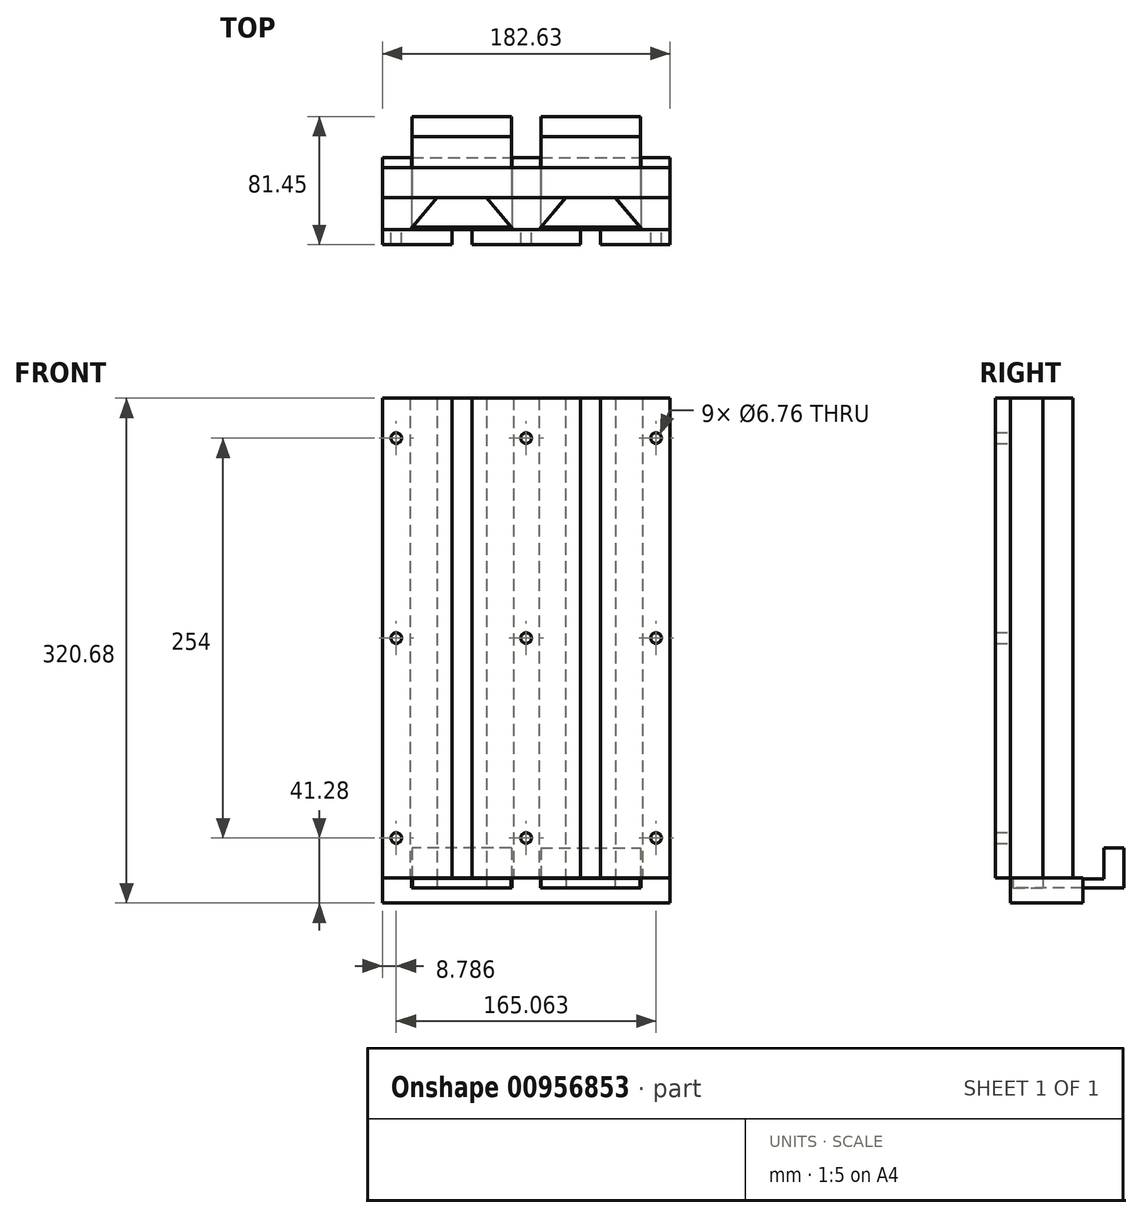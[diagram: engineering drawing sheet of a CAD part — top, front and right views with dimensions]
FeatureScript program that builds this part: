
annotation { "Feature Type Name" : "Feature", "Feature Type Description" : "" }
export const myFeature = defineFeature(function(context is Context, id is Id, definition is map)
    precondition{}
    {
        {
            var Q0;
            Q0=qCreatedBy(makeId("Top.planeOp"),FACE);
            var sketch = newSketch(context, id + "F0", { "sketchPlane" : qUnion([Q0])});
            skLineSegment(sketch, "E0", {"start": v(-15.74, -18.9) * mm, "end": v(0, 0) * mm});
            skLineSegment(sketch, "E1", {"start": v(0, 0) * mm, "end": v(31.27, 0) * mm});
            skLineSegment(sketch, "E2", {"start": v(31.27, 0) * mm, "end": v(47, -18.9) * mm});
            skLineSegment(sketch, "E3", {"start": v(47, -18.9) * mm, "end": v(-15.74, -18.9) * mm});
            skLineSegment(sketch, "E4", {"start": v(66.05, -18.9) * mm, "end": v(81.79, 0) * mm});
            skLineSegment(sketch, "E5", {"start": v(81.79, 0) * mm, "end": v(113.06, 0) * mm});
            skLineSegment(sketch, "E6", {"start": v(113.06, 0) * mm, "end": v(128.8, -18.9) * mm});
            skLineSegment(sketch, "E7", {"start": v(128.8, -18.9) * mm, "end": v(66.05, -18.9) * mm});
            skSolve(sketch);
        }
        {
            var Q0;
            Q0 = qSketchRegion(id + "F0", true);
            extrude(context, id + "F1", {"entities" : qUnion([Q0]), "depth" : 5.97 * mm, "offsetDistance" : 25.4 * mm});
        }
        {
            var Q0;
            Q0=makeQuery(id+"F1.opExtrude","CAP_FACE",FACE,{"disambiguationData":[OSD([sQuery(id+"F0.wireOp",EDGE,"E4"),sQuery(id+"F0.wireOp",EDGE,"E5"),sQuery(id+"F0.wireOp",EDGE,"E6"),sQuery(id+"F0.wireOp",EDGE,"E7")])],"isStart":true});
            var sketch = newSketch(context, id + "F2", { "sketchPlane" : qUnion([Q0])});
            skLineSegment(sketch, "E8.bottom", {"start": v(-34.79, 20.49) * mm, "end": v(147.84, 20.49) * mm});
            skLineSegment(sketch, "E8.top", {"start": v(-34.79, -25.4) * mm, "end": v(147.84, -25.4) * mm});
            skLineSegment(sketch, "E8.left", {"start": v(-34.79, 20.49) * mm, "end": v(-34.79, -25.4) * mm});
            skLineSegment(sketch, "E8.right", {"start": v(147.84, 20.49) * mm, "end": v(147.84, -25.4) * mm});
            skSolve(sketch);
        }
        {
            var Q0;
            Q0 = qSketchRegion(id + "F2", true);
            extrude(context, id + "F3", {"entities" : qUnion([Q0]), "depth" : 9.52 * mm, "offsetDistance" : 25.4 * mm});
        }
        {
            var Q0;
            Q0=makeQuery(id+"F1.opExtrude","SWEPT_FACE",FACE,{"disambiguationData":[OSD([sQuery(id+"F0.wireOp",EDGE,"E5")])]});
            var sketch = newSketch(context, id + "F4", { "sketchPlane" : qUnion([Q0])});
            skLineSegment(sketch, "E9.0", {"start": v(-128.8, 5.97) * mm, "end": v(-128.8, 0) * mm, "construction": true});
            skLineSegment(sketch, "E10.0", {"start": v(-113.06, 5.97) * mm, "end": v(-128.8, 5.97) * mm, "construction": true});
            skLineSegment(sketch, "E11.0", {"start": v(-81.79, 5.97) * mm, "end": v(-113.06, 5.97) * mm, "construction": true});
            skLineSegment(sketch, "E12.0", {"start": v(-66.05, 5.97) * mm, "end": v(-81.79, 5.97) * mm, "construction": true});
            skLineSegment(sketch, "E13.0", {"start": v(-66.05, 5.97) * mm, "end": v(-66.05, 0) * mm, "construction": true});
            skLineSegment(sketch, "E14.0", {"start": v(-47, 5.97) * mm, "end": v(-47, 0) * mm, "construction": true});
            skLineSegment(sketch, "E15.0", {"start": v(-31.27, 5.97) * mm, "end": v(-47, 5.97) * mm, "construction": true});
            skLineSegment(sketch, "E16.0", {"start": v(-31.27, 5.97) * mm, "end": v(-31.27, 0) * mm});
            skLineSegment(sketch, "E17.0", {"start": v(0, 5.97) * mm, "end": v(-31.27, 5.97) * mm, "construction": true});
            skLineSegment(sketch, "E18.0", {"start": v(15.74, 5.97) * mm, "end": v(0, 5.97) * mm, "construction": true});
            skLineSegment(sketch, "E19.0", {"start": v(15.74, 5.97) * mm, "end": v(15.74, 0) * mm, "construction": true});
            skLineSegment(sketch, "E20", {"start": v(-129.04, 0) * mm, "end": v(-129.04, 5.71) * mm});
            skLineSegment(sketch, "E21", {"start": v(-129.04, 5.71) * mm, "end": v(-65.8, 5.72) * mm});
            skLineSegment(sketch, "E22", {"start": v(-65.8, 5.72) * mm, "end": v(-65.8, 0) * mm});
            skLineSegment(sketch, "E23", {"start": v(-65.8, 0) * mm, "end": v(-129.04, 0) * mm});
            skLineSegment(sketch, "E24", {"start": v(-47.26, 0) * mm, "end": v(-47.26, 5.72) * mm});
            skLineSegment(sketch, "E25", {"start": v(-47.26, 5.72) * mm, "end": v(15.99, 5.72) * mm});
            skLineSegment(sketch, "E26", {"start": v(15.99, 5.72) * mm, "end": v(15.99, 0) * mm});
            skLineSegment(sketch, "E27", {"start": v(15.99, 0) * mm, "end": v(-47.26, 0) * mm});
            skSolve(sketch);
        }
        {
            var Q0;
            Q0 = qSketchRegion(id + "F4", true);
            extrude(context, id + "F5", {"entities" : qUnion([Q0]), "depth" : 25.4 * mm, "offsetDistance" : 25.4 * mm});
        }
        {
            var Q0;
            Q0=makeQuery(id+"F3.opExtrude","CAP_FACE",FACE,{"disambiguationData":[OSD([sQuery(id+"F2.wireOp",EDGE,"E8.bottom"),sQuery(id+"F2.wireOp",EDGE,"E8.top"),sQuery(id+"F2.wireOp",EDGE,"E8.left"),sQuery(id+"F2.wireOp",EDGE,"E8.right")])],"isStart":true});
            var sketch = newSketch(context, id + "F6", { "sketchPlane" : qUnion([Q0])});
            skLineSegment(sketch, "E28.bottom", {"start": v(-34.79, 25.4) * mm, "end": v(-16.24, 25.4) * mm});
            skLineSegment(sketch, "E28.top", {"start": v(-34.79, -20.49) * mm, "end": v(-16.24, -20.49) * mm});
            skLineSegment(sketch, "E28.left", {"start": v(-34.79, 25.4) * mm, "end": v(-34.79, -20.49) * mm});
            skLineSegment(sketch, "E28.right", {"start": v(-16.24, 25.4) * mm, "end": v(-16.24, -20.49) * mm});
            skLineSegment(sketch, "E29.bottom", {"start": v(147.84, 25.4) * mm, "end": v(129.3, 25.4) * mm});
            skLineSegment(sketch, "E29.top", {"start": v(147.84, -20.49) * mm, "end": v(129.3, -20.49) * mm});
            skLineSegment(sketch, "E29.left", {"start": v(147.84, 25.4) * mm, "end": v(147.84, -20.49) * mm});
            skLineSegment(sketch, "E29.right", {"start": v(129.3, 25.4) * mm, "end": v(129.3, -20.49) * mm});
            skLineSegment(sketch, "E30.bottom", {"start": v(47.51, 25.4) * mm, "end": v(65.54, 25.4) * mm});
            skLineSegment(sketch, "E30.top", {"start": v(47.51, -20.49) * mm, "end": v(65.54, -20.49) * mm});
            skLineSegment(sketch, "E30.left", {"start": v(47.51, 25.4) * mm, "end": v(47.51, -20.49) * mm});
            skLineSegment(sketch, "E30.right", {"start": v(65.54, 25.4) * mm, "end": v(65.54, -20.49) * mm});
            skSolve(sketch);
        }
        {
            var Q0;
            Q0 = qSketchRegion(id + "F6", true);
            extrude(context, id + "F7", {"entities" : qUnion([Q0]), "operationType" : NewBodyOperationType.ADD, "depth" : 6.35 * mm, "offsetDistance" : 25.4 * mm});
        }
        {
            var Q0;
            Q0=makeQuery(id+"F7.opExtrude","CAP_FACE",FACE,{"disambiguationData":[OSD([sQuery(id+"F6.wireOp",EDGE,"E30.bottom"),sQuery(id+"F6.wireOp",EDGE,"E30.top"),sQuery(id+"F6.wireOp",EDGE,"E30.left"),sQuery(id+"F6.wireOp",EDGE,"E30.right")])],"isStart":false});
            var sketch = newSketch(context, id + "F8", { "sketchPlane" : qUnion([Q0])});
            skLineSegment(sketch, "E31.0", {"start": v(-34.79, -20.49) * mm, "end": v(-34.79, 25.4) * mm, "construction": true});
            skLineSegment(sketch, "E32.0", {"start": v(147.84, -20.49) * mm, "end": v(147.84, 25.4) * mm, "construction": true});
            skLineSegment(sketch, "E33.0", {"start": v(-34.79, 25.4) * mm, "end": v(-16.24, 25.4) * mm, "construction": true});
            skLineSegment(sketch, "E34.0", {"start": v(129.3, 25.4) * mm, "end": v(147.84, 25.4) * mm, "construction": true});
            skPoint(sketch, "E35.0", {"position": v(56.53, 25.4) * mm});
            skLineSegment(sketch, "E36.bottom", {"start": v(-34.79, 19.05) * mm, "end": v(147.84, 19.05) * mm});
            skLineSegment(sketch, "E36.top", {"start": v(-34.79, 0) * mm, "end": v(147.84, 0) * mm});
            skLineSegment(sketch, "E36.left", {"start": v(-34.79, 19.05) * mm, "end": v(-34.79, 0) * mm});
            skLineSegment(sketch, "E36.right", {"start": v(147.84, 19.05) * mm, "end": v(147.84, 0) * mm});
            skSolve(sketch);
        }
        {
            var Q0;
            Q0 = qSketchRegion(id + "F8", true);
            extrude(context, id + "F9", {"entities" : qUnion([Q0]), "depth" : 304.8 * mm, "offsetDistance" : 25.4 * mm});
        }
        {
            var Q0;
            Q0=makeQuery(id+"F5.opExtrude","SWEPT_FACE",FACE,{"disambiguationData":[OSD([sQuery(id+"F4.wireOp",EDGE,"E26")])]});
            var sketch = newSketch(context, id + "F10", { "sketchPlane" : qUnion([Q0])});
            skLineSegment(sketch, "E37.bottom", {"start": v(-51.44, 25.4) * mm, "end": v(-38.74, 25.4) * mm});
            skLineSegment(sketch, "E37.top", {"start": v(-51.44, 0) * mm, "end": v(-38.74, 0) * mm});
            skLineSegment(sketch, "E37.left", {"start": v(-51.44, 25.4) * mm, "end": v(-51.44, 0) * mm});
            skLineSegment(sketch, "E37.right", {"start": v(-38.74, 25.4) * mm, "end": v(-38.74, 5.72) * mm});
            skLineSegment(sketch, "E38.bottom", {"start": v(-38.74, 0) * mm, "end": v(-25.4, 0) * mm});
            skLineSegment(sketch, "E38.top", {"start": v(-38.74, 5.72) * mm, "end": v(-25.4, 5.72) * mm});
            skLineSegment(sketch, "E38.right", {"start": v(-25.4, 0) * mm, "end": v(-25.4, 5.72) * mm});
            skSolve(sketch);
        }
        {
            var Q0;
            Q0 = qSketchRegion(id + "F10", true);
            var Q1;
            Q1=makeQuery(id+"F5.opExtrude","SWEPT_FACE",FACE,{"disambiguationData":[OSD([sQuery(id+"F4.wireOp",EDGE,"E24")])]});
            extrude(context, id + "F11", {"entities" : qUnion([Q0]), "operationType" : NewBodyOperationType.ADD, "endBound" : BoundingType.UP_TO_SURFACE, "oppositeDirection" : true, "depth" : 25.4 * mm, "endBoundEntityFace" : qUnion([Q1]), "offsetDistance" : 25.4 * mm});
        }
        {
            var Q0;
            Q0=makeQuery(id+"F5.opExtrude","SWEPT_FACE",FACE,{"disambiguationData":[OSD([sQuery(id+"F4.wireOp",EDGE,"E20")])]});
            var sketch = newSketch(context, id + "F12", { "sketchPlane" : qUnion([Q0])});
            skLineSegment(sketch, "E39.0", {"start": v(38.74, 5.72) * mm, "end": v(25.4, 5.72) * mm});
            skLineSegment(sketch, "E39.1", {"start": v(38.74, 0) * mm, "end": v(25.4, 0) * mm});
            skLineSegment(sketch, "E39.2", {"start": v(51.44, 0) * mm, "end": v(38.74, 0) * mm});
            skLineSegment(sketch, "E39.3", {"start": v(25.4, 0) * mm, "end": v(25.4, 5.72) * mm});
            skLineSegment(sketch, "E39.4", {"start": v(51.44, 25.4) * mm, "end": v(51.44, 0) * mm});
            skLineSegment(sketch, "E39.5", {"start": v(38.74, 25.4) * mm, "end": v(38.74, 5.72) * mm});
            skLineSegment(sketch, "E39.6", {"start": v(51.44, 25.4) * mm, "end": v(38.74, 25.4) * mm});
            skSolve(sketch);
        }
        {
            var Q0;
            Q0 = qSketchRegion(id + "F12", true);
            var Q1;
            Q1=makeQuery(id+"F5.opExtrude","SWEPT_FACE",FACE,{"disambiguationData":[OSD([sQuery(id+"F4.wireOp",EDGE,"E22")])]});
            extrude(context, id + "F13", {"entities" : qUnion([Q0]), "operationType" : NewBodyOperationType.ADD, "endBound" : BoundingType.UP_TO_SURFACE, "oppositeDirection" : true, "depth" : 25.4 * mm, "endBoundEntityFace" : qUnion([Q1]), "offsetDistance" : 25.4 * mm});
        }
        {
            var Q0;
            Q0=makeQuery(id+"F7.opExtrude","CAP_FACE",FACE,{"disambiguationData":[OSD([sQuery(id+"F6.wireOp",EDGE,"E30.bottom"),sQuery(id+"F6.wireOp",EDGE,"E30.top"),sQuery(id+"F6.wireOp",EDGE,"E30.left"),sQuery(id+"F6.wireOp",EDGE,"E30.right")])],"isStart":false});
            var sketch = newSketch(context, id + "F14", { "sketchPlane" : qUnion([Q0])});
            skLineSegment(sketch, "E40", {"start": v(-34.79, 0) * mm, "end": v(-34.79, -20.49) * mm});
            skLineSegment(sketch, "E41", {"start": v(-34.79, -20.49) * mm, "end": v(-17.22, -20.49) * mm});
            skLineSegment(sketch, "E42", {"start": v(-17.22, -20.49) * mm, "end": v(-0.17, 0) * mm});
            skLineSegment(sketch, "E43", {"start": v(-0.17, 0) * mm, "end": v(-34.79, 0) * mm});
            skLineSegment(sketch, "E44", {"start": v(56.53, 25.4) * mm, "end": v(56.53, -20.49) * mm, "construction": true});
            skLineSegment(sketch, "E45", {"start": v(31.43, 0) * mm, "end": v(48.49, -20.49) * mm});
            skLineSegment(sketch, "E46", {"start": v(48.49, -20.49) * mm, "end": v(56.53, -20.49) * mm});
            skLineSegment(sketch, "E47", {"start": v(56.53, 0) * mm, "end": v(31.43, 0) * mm});
            skLineSegment(sketch, "E48.MirrorCS", {"start": v(64.57, -20.49) * mm, "end": v(56.53, -20.49) * mm});
            skLineSegment(sketch, "E49.MirrorCS", {"start": v(56.53, 0) * mm, "end": v(81.62, 0) * mm});
            skLineSegment(sketch, "E50.MirrorCS", {"start": v(81.62, 0) * mm, "end": v(64.57, -20.49) * mm});
            skLineSegment(sketch, "E51.MirrorCS", {"start": v(130.28, -20.49) * mm, "end": v(113.22, 0) * mm});
            skLineSegment(sketch, "E52.MirrorCS", {"start": v(147.84, -20.49) * mm, "end": v(130.28, -20.49) * mm});
            skLineSegment(sketch, "E53.MirrorCS", {"start": v(113.22, 0) * mm, "end": v(147.84, 0) * mm});
            skLineSegment(sketch, "E54.MirrorCS", {"start": v(147.84, 0) * mm, "end": v(147.84, -20.49) * mm});
            skSolve(sketch);
        }
        {
            var Q0;
            Q0 = qSketchRegion(id + "F14", true);
            extrude(context, id + "F15", {"entities" : qUnion([Q0]), "depth" : 304.8 * mm, "offsetDistance" : 25.4 * mm});
        }
        {
            var Q0;
            Q0=makeQuery(id+"F15.opExtrude","SWEPT_FACE",FACE,{"disambiguationData":[OSD([sQuery(id+"F14.wireOp",EDGE,"E41")])]});
            var sketch = newSketch(context, id + "F16", { "sketchPlane" : qUnion([Q0])});
            skLineSegment(sketch, "E55.bottom", {"start": v(-34.79, 311.15) * mm, "end": v(9.28, 311.15) * mm});
            skLineSegment(sketch, "E55.top", {"start": v(-34.79, 6.35) * mm, "end": v(9.28, 6.35) * mm});
            skLineSegment(sketch, "E55.left", {"start": v(-34.79, 311.15) * mm, "end": v(-34.79, 6.35) * mm});
            skLineSegment(sketch, "E55.right", {"start": v(9.28, 311.15) * mm, "end": v(9.28, 6.35) * mm});
            skLineSegment(sketch, "E56.bottom", {"start": v(21.98, 311.15) * mm, "end": v(91.07, 311.15) * mm});
            skLineSegment(sketch, "E56.top", {"start": v(21.98, 6.35) * mm, "end": v(91.07, 6.35) * mm});
            skLineSegment(sketch, "E56.left", {"start": v(21.98, 311.15) * mm, "end": v(21.98, 6.35) * mm});
            skLineSegment(sketch, "E56.right", {"start": v(91.07, 311.15) * mm, "end": v(91.07, 6.35) * mm});
            skLineSegment(sketch, "E57.bottom", {"start": v(103.77, 311.15) * mm, "end": v(147.84, 311.15) * mm});
            skLineSegment(sketch, "E57.top", {"start": v(103.77, 6.35) * mm, "end": v(147.84, 6.35) * mm});
            skLineSegment(sketch, "E57.left", {"start": v(103.77, 311.15) * mm, "end": v(103.77, 6.35) * mm});
            skLineSegment(sketch, "E57.right", {"start": v(147.84, 311.15) * mm, "end": v(147.84, 6.35) * mm});
            skPoint(sketch, "E58", {"position": v(56.53, 311.15) * mm});
            skLineSegment(sketch, "E59.0.0", {"start": v(48.49, 6.35) * mm, "end": v(64.57, 6.35) * mm, "construction": true});
            skLineSegment(sketch, "E59.0.1", {"start": v(64.57, 6.35) * mm, "end": v(64.57, 311.15) * mm, "construction": true});
            skLineSegment(sketch, "E59.0.2", {"start": v(64.57, 311.15) * mm, "end": v(48.49, 311.15) * mm, "construction": true});
            skLineSegment(sketch, "E59.0.3", {"start": v(48.49, 311.15) * mm, "end": v(48.49, 6.35) * mm, "construction": true});
            skLineSegment(sketch, "E60.0", {"start": v(-17.22, 311.15) * mm, "end": v(-0.17, 311.15) * mm, "construction": true});
            skLineSegment(sketch, "E61.0", {"start": v(31.43, 311.15) * mm, "end": v(48.49, 311.15) * mm, "construction": true});
            skLineSegment(sketch, "E62.0", {"start": v(81.62, 311.15) * mm, "end": v(64.57, 311.15) * mm, "construction": true});
            skLineSegment(sketch, "E63.0", {"start": v(130.28, 311.15) * mm, "end": v(113.22, 311.15) * mm, "construction": true});
            skLineSegment(sketch, "E64", {"start": v(-0.17, 311.15) * mm, "end": v(31.43, 311.15) * mm, "construction": true});
            skPoint(sketch, "E65", {"position": v(15.63, 311.15) * mm});
            skPoint(sketch, "E66", {"position": v(91.07, 311.15) * mm});
            skLineSegment(sketch, "E67", {"start": v(81.62, 311.15) * mm, "end": v(113.22, 311.15) * mm, "construction": true});
            skPoint(sketch, "E68", {"position": v(97.42, 311.15) * mm});
            skCircle(sketch, "E69", {"center": v(-26, 285.75) * mm, "radius": 3.38 * mm});
            skCircle(sketch, "E70", {"center": v(-26, 158.75) * mm, "radius": 3.38 * mm});
            skCircle(sketch, "E71", {"center": v(-26, 31.75) * mm, "radius": 3.38 * mm});
            skCircle(sketch, "E72", {"center": v(56.53, 31.75) * mm, "radius": 3.38 * mm});
            skCircle(sketch, "E73", {"center": v(56.53, 158.75) * mm, "radius": 3.38 * mm});
            skCircle(sketch, "E74", {"center": v(56.53, 285.75) * mm, "radius": 3.38 * mm});
            skCircle(sketch, "E75", {"center": v(139.06, 285.75) * mm, "radius": 3.38 * mm});
            skCircle(sketch, "E76", {"center": v(139.06, 158.75) * mm, "radius": 3.38 * mm});
            skCircle(sketch, "E77", {"center": v(139.06, 31.75) * mm, "radius": 3.38 * mm});
            skLineSegment(sketch, "E78", {"start": v(-26, 31.75) * mm, "end": v(56.53, 31.75) * mm, "construction": true});
            skLineSegment(sketch, "E79", {"start": v(56.53, 31.75) * mm, "end": v(139.06, 31.75) * mm, "construction": true});
            skLineSegment(sketch, "E80", {"start": v(139.06, 158.75) * mm, "end": v(56.53, 158.75) * mm, "construction": true});
            skLineSegment(sketch, "E81", {"start": v(56.53, 158.75) * mm, "end": v(-26, 158.75) * mm, "construction": true});
            skLineSegment(sketch, "E82", {"start": v(-26, 285.75) * mm, "end": v(56.53, 285.75) * mm, "construction": true});
            skLineSegment(sketch, "E83", {"start": v(56.53, 285.75) * mm, "end": v(139.06, 285.75) * mm, "construction": true});
            skLineSegment(sketch, "E84", {"start": v(-26, 311.15) * mm, "end": v(-26, 6.35) * mm, "construction": true});
            skLineSegment(sketch, "E85", {"start": v(56.53, 311.15) * mm, "end": v(56.53, 6.35) * mm, "construction": true});
            skLineSegment(sketch, "E86.0.0", {"start": v(130.28, 6.35) * mm, "end": v(147.84, 6.35) * mm, "construction": true});
            skLineSegment(sketch, "E86.0.1", {"start": v(147.84, 6.35) * mm, "end": v(147.84, 311.15) * mm, "construction": true});
            skLineSegment(sketch, "E86.0.2", {"start": v(147.84, 311.15) * mm, "end": v(130.28, 311.15) * mm, "construction": true});
            skLineSegment(sketch, "E86.0.3", {"start": v(130.28, 311.15) * mm, "end": v(130.28, 6.35) * mm, "construction": true});
            skPoint(sketch, "E87", {"position": v(139.06, 311.15) * mm});
            skLineSegment(sketch, "E88", {"start": v(139.06, 311.15) * mm, "end": v(139.06, 6.35) * mm, "construction": true});
            skLineSegment(sketch, "E89", {"start": v(-34.79, 158.75) * mm, "end": v(-26, 158.75) * mm, "construction": true});
            skSolve(sketch);
        }
        {
            var Q0;
            Q0 = qSketchRegion(id + "F16", true);
            extrude(context, id + "F17", {"entities" : qUnion([Q0]), "depth" : 9.52 * mm, "offsetDistance" : 25.4 * mm});
        }
    });
